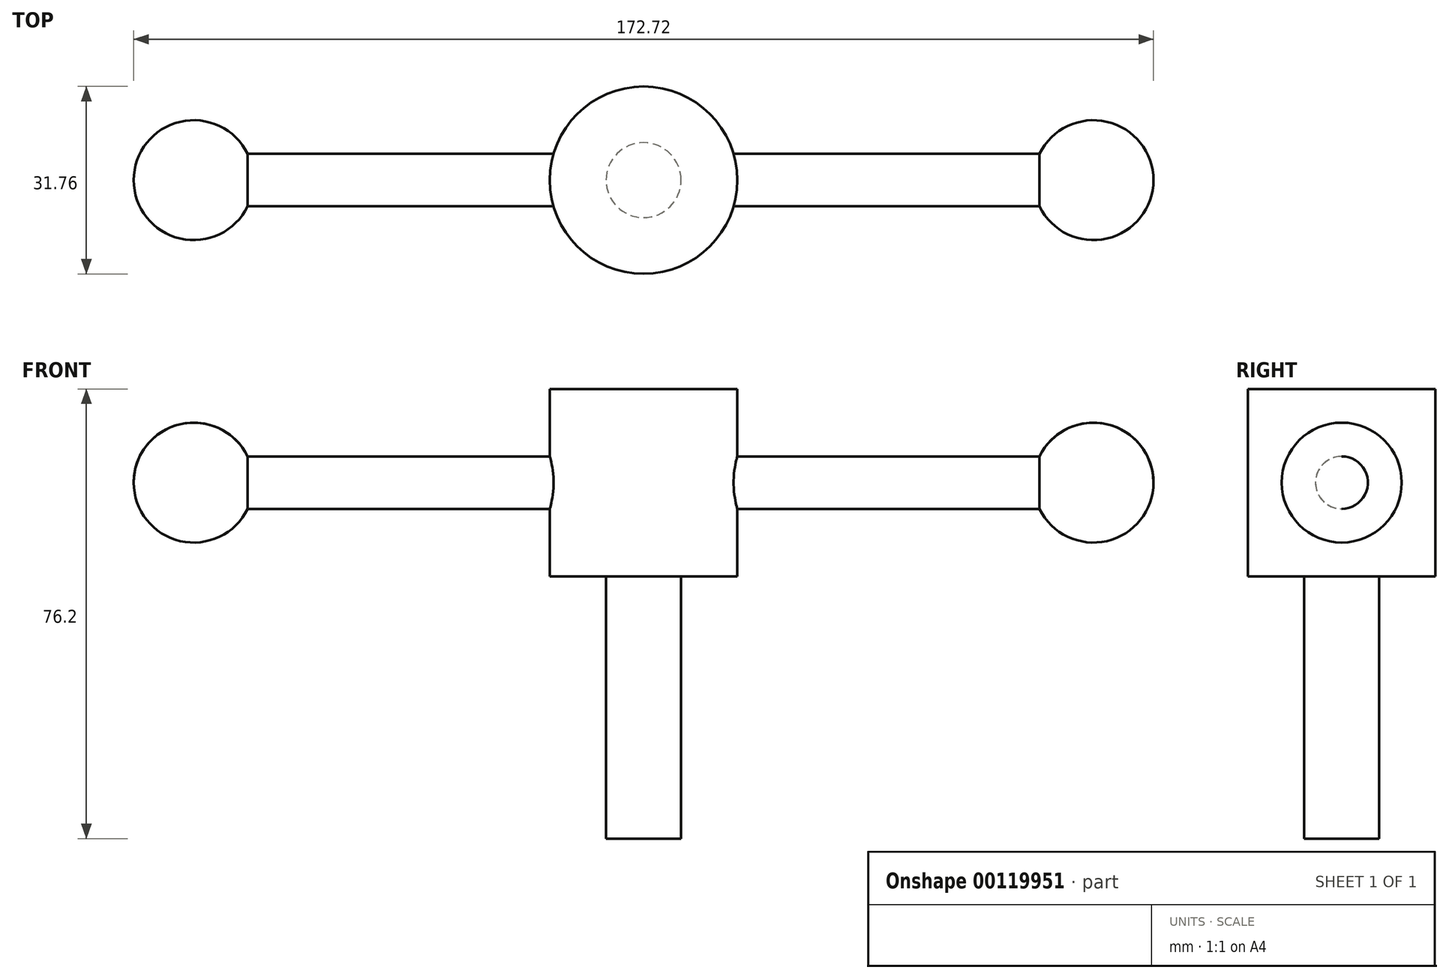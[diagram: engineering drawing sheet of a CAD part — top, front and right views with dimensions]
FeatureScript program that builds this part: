
annotation { "Feature Type Name" : "Feature", "Feature Type Description" : "" }
export const myFeature = defineFeature(function(context is Context, id is Id, definition is map)
    precondition{}
    {
        {
            var Q0;
            Q0=qCreatedBy(makeId("Top.planeOp"),FACE);
            var sketch = newSketch(context, id + "F0", { "sketchPlane" : qUnion([Q0])});
            skCircle(sketch, "E0", {"center": v(0, 0) * mm, "radius": 15.88 * mm});
            skSolve(sketch);
        }
        {
            var Q0;
            Q0 = qSketchRegion(id + "F0", true);
            extrude(context, id + "F1", {"entities" : qUnion([Q0]), "depth" : 31.75 * mm});
        }
        {
            var Q0;
            Q0=qCreatedBy(makeId("Top.planeOp"),FACE);
            var sketch = newSketch(context, id + "F2", { "sketchPlane" : qUnion([Q0])});
            skCircle(sketch, "E1", {"center": v(0, 0) * mm, "radius": 6.35 * mm});
            skSolve(sketch);
        }
        {
            var Q0;
            Q0 = qSketchRegion(id + "F2", true);
            extrude(context, id + "F3", {"entities" : qUnion([Q0]), "operationType" : NewBodyOperationType.ADD, "oppositeDirection" : true, "depth" : 44.45 * mm});
        }
        {
            var Q0;
            Q0=qCreatedBy(makeId("Right.planeOp"),FACE);
            var sketch = newSketch(context, id + "F4", { "sketchPlane" : qUnion([Q0])});
            skLineSegment(sketch, "E2", {"start": v(0, 0) * mm, "end": v(0, 15.88) * mm, "construction": true});
            skCircle(sketch, "E3", {"center": v(0, 15.88) * mm, "radius": 4.45 * mm});
            skSolve(sketch);
        }
        {
            var Q0;
            Q0 = qSketchRegion(id + "F4", true);
            extrude(context, id + "F5", {"entities" : qUnion([Q0]), "operationType" : NewBodyOperationType.ADD, "depth" : 76.2 * mm});
        }
        {
            var Q0;
            Q0=qCreatedBy(makeId("Right.planeOp"),FACE);
            var sketch = newSketch(context, id + "F6", { "sketchPlane" : qUnion([Q0])});
            skCircle(sketch, "E4", {"center": v(0, 15.88) * mm, "radius": 4.45 * mm});
            skSolve(sketch);
        }
        {
            var Q0;
            Q0 = qSketchRegion(id + "F6", true);
            extrude(context, id + "F7", {"entities" : qUnion([Q0]), "operationType" : NewBodyOperationType.ADD, "oppositeDirection" : true, "depth" : 76.2 * mm});
        }
        {
            var Q0;
            Q0=qCreatedBy(makeId("Front.planeOp"),FACE);
            var sketch = newSketch(context, id + "F8", { "sketchPlane" : qUnion([Q0])});
            skArc(sketch, "E5", {"start": v(-66.04, 15.88) * mm, "mid": v(-76.2, 26.04) * mm, "end": v(-86.36, 15.88) * mm});
            skArc(sketch, "E6", {"start": v(66.04, 15.88) * mm, "mid": v(76.2, 26.04) * mm, "end": v(86.36, 15.88) * mm});
            skLineSegment(sketch, "E7", {"start": v(-76.2, 15.88) * mm, "end": v(76.2, 15.88) * mm, "construction": true});
            skLineSegment(sketch, "E8", {"start": v(-86.36, 15.88) * mm, "end": v(-66.04, 15.88) * mm});
            skLineSegment(sketch, "E9", {"start": v(66.04, 15.88) * mm, "end": v(86.36, 15.88) * mm});
            skSolve(sketch);
        }
        {
            var Q0;
            Q0 = qSketchRegion(id + "F8", true);
            var Q1;
            Q1=sQuery(id+"F8.wireOp",EDGE,"E7");
            revolve(context, id + "F9", {"operationType" : NewBodyOperationType.ADD, "entities" : qUnion([Q0]), "axis" : qUnion([Q1]), "revolveType" : RevolveType.FULL});
        }
    });
